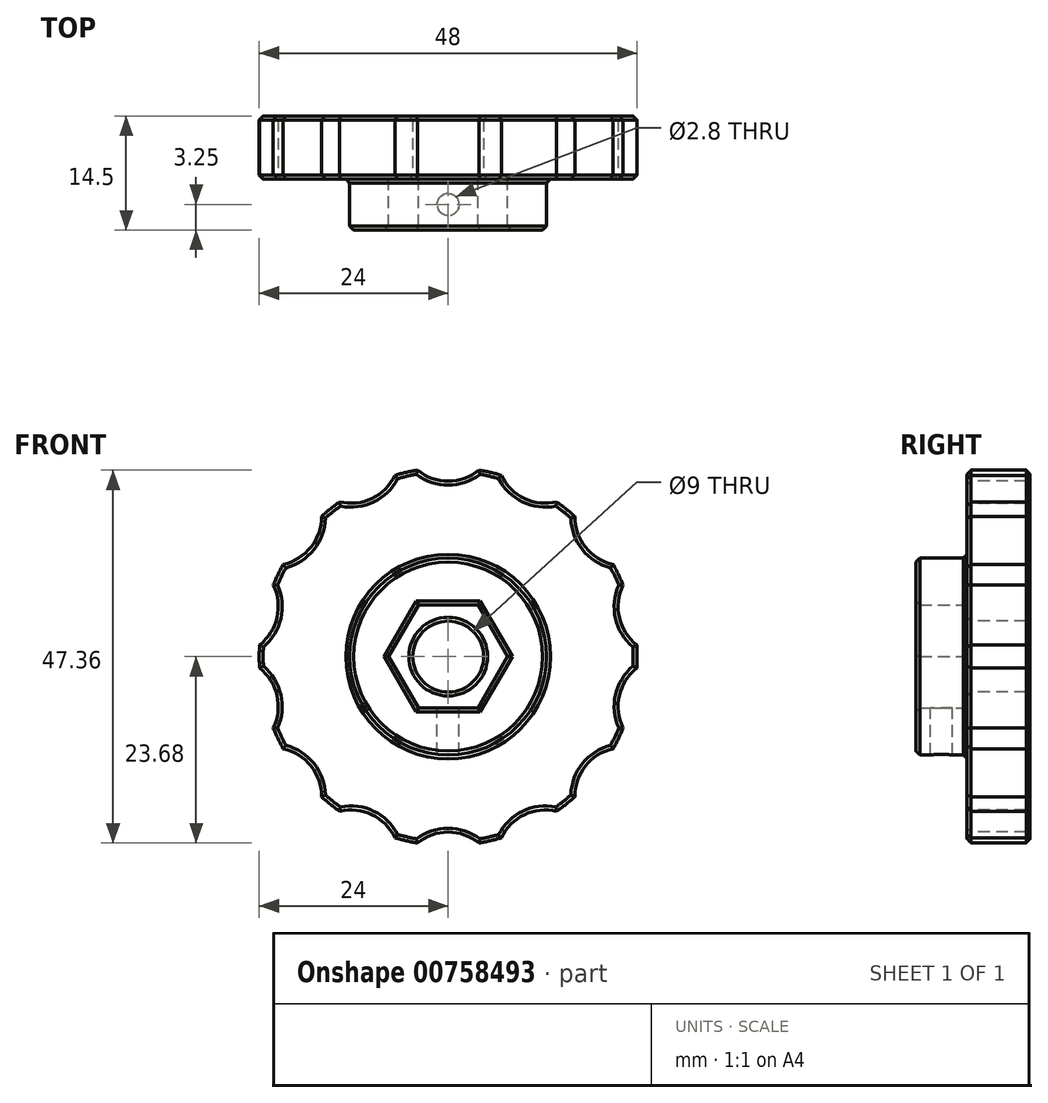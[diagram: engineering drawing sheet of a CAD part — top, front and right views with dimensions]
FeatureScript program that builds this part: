
annotation { "Feature Type Name" : "Feature", "Feature Type Description" : "" }
export const myFeature = defineFeature(function(context is Context, id is Id, definition is map)
    precondition{}
    {
        {
            var Q0;
            Q0=qCreatedBy(makeId("Front.planeOp"),FACE);
            var sketch = newSketch(context, id + "F0", { "sketchPlane" : qUnion([Q0])});
            skCircle(sketch, "E0", {"center": v(0, 0) * mm, "radius": 24 * mm});
            skCircle(sketch, "E1.cCircle", {"center": v(0, 0) * mm, "radius": 6.55 * mm, "construction": true});
            skLineSegment(sketch, "E1.0", {"start": v(-3.78, 6.55) * mm, "end": v(3.78, 6.55) * mm});
            skLineSegment(sketch, "E1.1", {"start": v(3.78, 6.55) * mm, "end": v(7.56, 0) * mm});
            skLineSegment(sketch, "E1.2", {"start": v(7.56, 0) * mm, "end": v(3.78, -6.55) * mm});
            skLineSegment(sketch, "E1.3", {"start": v(3.78, -6.55) * mm, "end": v(-3.78, -6.55) * mm});
            skLineSegment(sketch, "E1.4", {"start": v(-3.78, -6.55) * mm, "end": v(-7.56, 0) * mm});
            skLineSegment(sketch, "E1.5", {"start": v(-7.56, 0) * mm, "end": v(-3.78, 6.55) * mm});
            skPoint(sketch, "E1.0.midPoint", {"position": v(0, 6.55) * mm});
            skCircle(sketch, "E2", {"center": v(0, 0) * mm, "radius": 12.5 * mm});
            skCircle(sketch, "E3", {"center": v(0, 0) * mm, "radius": 4.5 * mm});
            skArc(sketch, "E4", {"start": v(-3.9, 23.68) * mm, "mid": v(0, 22.3) * mm, "end": v(3.9, 23.68) * mm});
            skArc(sketch, "E5.1.0", {"start": v(-13.79, 19.64) * mm, "mid": v(-9.68, 20.1) * mm, "end": v(-6.76, 23.03) * mm});
            skArc(sketch, "E5.2.0", {"start": v(-20.95, 11.72) * mm, "mid": v(-17.44, 13.9) * mm, "end": v(-16.08, 17.81) * mm});
            skArc(sketch, "E5.3.0", {"start": v(-23.96, 1.47) * mm, "mid": v(-21.74, 4.96) * mm, "end": v(-22.22, 9.07) * mm});
            skArc(sketch, "E5.4.0", {"start": v(-22.22, -9.07) * mm, "mid": v(-21.74, -4.96) * mm, "end": v(-23.96, -1.47) * mm});
            skArc(sketch, "E5.5.0", {"start": v(-16.08, -17.81) * mm, "mid": v(-17.44, -13.9) * mm, "end": v(-20.95, -11.72) * mm});
            skArc(sketch, "E5.6.0", {"start": v(-6.76, -23.03) * mm, "mid": v(-9.68, -20.1) * mm, "end": v(-13.79, -19.64) * mm});
            skArc(sketch, "E5.7.0", {"start": v(3.9, -23.68) * mm, "mid": v(0, -22.3) * mm, "end": v(-3.9, -23.68) * mm});
            skArc(sketch, "E5.8.0", {"start": v(13.79, -19.64) * mm, "mid": v(9.68, -20.1) * mm, "end": v(6.76, -23.03) * mm});
            skArc(sketch, "E5.9.0", {"start": v(20.95, -11.72) * mm, "mid": v(17.44, -13.9) * mm, "end": v(16.08, -17.81) * mm});
            skArc(sketch, "E5.10.0", {"start": v(23.96, -1.47) * mm, "mid": v(21.74, -4.96) * mm, "end": v(22.22, -9.07) * mm});
            skArc(sketch, "E5.11.0", {"start": v(22.22, 9.07) * mm, "mid": v(21.74, 4.96) * mm, "end": v(23.96, 1.47) * mm});
            skArc(sketch, "E5.12.0", {"start": v(16.08, 17.81) * mm, "mid": v(17.44, 13.9) * mm, "end": v(20.95, 11.72) * mm});
            skArc(sketch, "E5.13.0", {"start": v(6.76, 23.03) * mm, "mid": v(9.68, 20.1) * mm, "end": v(13.79, 19.64) * mm});
            skSolve(sketch);
        }
        {
            var Q0;
            Q0=makeQuery(id+"F0.imprint","IMPRINT",FACE,{"disambiguationData":[TD([[makeQuery(id+"F0.imprint","IMPRINT",EDGE,{"derivedFrom":sQuery(id+"F0.wireOp",EDGE,"E2")}),-1.0]])]});
            var Q1;
            Q1=makeQuery(id+"F0.imprint","IMPRINT",FACE,{"disambiguationData":[TD([[makeQuery(id+"F0.imprint","IMPRINT",EDGE,{"derivedFrom":sQuery(id+"F0.wireOp",EDGE,"E1.0")}),1.0]])]});
            var Q2;
            Q2=makeQuery(id+"F0.imprint","IMPRINT",FACE,{"disambiguationData":[TD([[makeQuery(id+"F0.imprint","IMPRINT",EDGE,{"derivedFrom":sQuery(id+"F0.wireOp",EDGE,"E1.0")}),-1.0]])]});
            extrude(context, id + "F1", {"entities" : qUnion([Q0, Q1, Q2]), "oppositeDirection" : true, "depth" : (15 - 6.5 - 0.5) * mm, "offsetDistance" : 25 * mm});
        }
        {
            var Q0;
            Q0=makeQuery(id+"F0.imprint","IMPRINT",FACE,{"disambiguationData":[TD([[makeQuery(id+"F0.imprint","IMPRINT",EDGE,{"derivedFrom":sQuery(id+"F0.wireOp",EDGE,"E1.0")}),1.0]])]});
            extrude(context, id + "F2", {"entities" : qUnion([Q0]), "operationType" : NewBodyOperationType.ADD, "depth" : 6.5 * mm, "offsetDistance" : 25 * mm});
        }
        {
            var Q0;
            Q0=makeQuery(id+"F2.opExtrude","SWEPT_FACE",FACE,{"disambiguationData":[OSD([sQuery(id+"F0.wireOp",EDGE,"E1.3")])]});
            var sketch = newSketch(context, id + "F3", { "sketchPlane" : qUnion([Q0])});
            skPoint(sketch, "E6", {"position": v(0, -3.25) * mm});
            skSolve(sketch);
        }
        {
            var Q0;
            Q0=sQuery(id+"F3.wireOp",VERTEX,"E6");
            var Q1;
            Q1=makeQuery(id+"F1.opExtrude","SWEPT_BODY",BODY,{"disambiguationData":[OSD([sQuery(id+"F0.wireOp",EDGE,"E0"),sQuery(id+"F0.wireOp",EDGE,"E3"),sQuery(id+"F0.wireOp",EDGE,"E4"),sQuery(id+"F0.wireOp",EDGE,"E5.1.0"),sQuery(id+"F0.wireOp",EDGE,"E5.2.0"),sQuery(id+"F0.wireOp",EDGE,"E5.3.0"),sQuery(id+"F0.wireOp",EDGE,"E5.4.0"),sQuery(id+"F0.wireOp",EDGE,"E5.5.0"),sQuery(id+"F0.wireOp",EDGE,"E5.6.0"),sQuery(id+"F0.wireOp",EDGE,"E5.7.0"),sQuery(id+"F0.wireOp",EDGE,"E5.8.0"),sQuery(id+"F0.wireOp",EDGE,"E5.9.0"),sQuery(id+"F0.wireOp",EDGE,"E5.10.0"),sQuery(id+"F0.wireOp",EDGE,"E5.11.0"),sQuery(id+"F0.wireOp",EDGE,"E5.12.0"),sQuery(id+"F0.wireOp",EDGE,"E5.13.0")])]});
            hole(context, id + "F4", {"style" : HoleStyle.SIMPLE, "endStyle" : HoleEndStyle.THROUGH, "holeDiameter" : 2.8 * mm, "majorDiameter" : 5 * mm, "isTappedThrough" : true, "tappedDepth" : 12 * mm, "tapClearance" : 3, "locations" : qUnion([Q0]), "scope" : qUnion([Q1])});
        }
        {
            var Q0;
            {var subQ0=sQuery(id+"F0.wireOp",EDGE,"E5.7.0");var subQ1=sQuery(id+"F0.wireOp",EDGE,"E5.5.0");var subQ2=sQuery(id+"F0.wireOp",EDGE,"E5.4.0");var subQ3=sQuery(id+"F0.wireOp",EDGE,"E5.3.0");var subQ4=sQuery(id+"F0.wireOp",EDGE,"E5.2.0");var subQ5=sQuery(id+"F0.wireOp",EDGE,"E5.1.0");var subQ6=sQuery(id+"F0.wireOp",EDGE,"E4");var subQ7=sQuery(id+"F0.wireOp",EDGE,"E5.10.0");var subQ8=sQuery(id+"F0.wireOp",EDGE,"E0");var subQ9=sQuery(id+"F0.wireOp",EDGE,"E5.11.0");var subQ10=sQuery(id+"F0.wireOp",EDGE,"E5.9.0");var subQ11=sQuery(id+"F0.wireOp",EDGE,"E5.8.0");var subQ12=sQuery(id+"F0.wireOp",EDGE,"E5.13.0");var subQ13=sQuery(id+"F0.wireOp",EDGE,"E5.12.0");var subQ14=sQuery(id+"F0.wireOp",EDGE,"E5.6.0");Q0=makeQuery(id+"F2.boolean.opBoolean","SPLIT",FACE,{"disambiguationData":[TD([makeQuery(id+"F1.opExtrude","SWEPT_FACE",FACE,{"disambiguationData":[OSD([subQ6])]})])],"derivedFrom":makeQuery(id+"F1.opExtrude","CAP_FACE",FACE,{"disambiguationData":[OSD([subQ8,sQuery(id+"F0.wireOp",EDGE,"E3"),subQ6,subQ5,subQ4,subQ3,subQ2,subQ1,subQ14,subQ0,subQ11,subQ10,subQ7,subQ9,subQ13,subQ12])],"isStart":true})});}
            var Q1;
            Q1=makeQuery(id+"F1.opExtrude","CAP_FACE",FACE,{"disambiguationData":[OSD([sQuery(id+"F0.wireOp",EDGE,"E0"),sQuery(id+"F0.wireOp",EDGE,"E3"),sQuery(id+"F0.wireOp",EDGE,"E4"),sQuery(id+"F0.wireOp",EDGE,"E5.1.0"),sQuery(id+"F0.wireOp",EDGE,"E5.2.0"),sQuery(id+"F0.wireOp",EDGE,"E5.3.0"),sQuery(id+"F0.wireOp",EDGE,"E5.4.0"),sQuery(id+"F0.wireOp",EDGE,"E5.5.0"),sQuery(id+"F0.wireOp",EDGE,"E5.6.0"),sQuery(id+"F0.wireOp",EDGE,"E5.7.0"),sQuery(id+"F0.wireOp",EDGE,"E5.8.0"),sQuery(id+"F0.wireOp",EDGE,"E5.9.0"),sQuery(id+"F0.wireOp",EDGE,"E5.10.0"),sQuery(id+"F0.wireOp",EDGE,"E5.11.0"),sQuery(id+"F0.wireOp",EDGE,"E5.12.0"),sQuery(id+"F0.wireOp",EDGE,"E5.13.0")])],"isStart":false});
            var Q2;
            Q2=makeQuery(id+"F2.opExtrude","CAP_FACE",FACE,{"disambiguationData":[OSD([sQuery(id+"F0.wireOp",EDGE,"E1.0"),sQuery(id+"F0.wireOp",EDGE,"E1.1"),sQuery(id+"F0.wireOp",EDGE,"E1.2"),sQuery(id+"F0.wireOp",EDGE,"E1.3"),sQuery(id+"F0.wireOp",EDGE,"E1.4"),sQuery(id+"F0.wireOp",EDGE,"E1.5"),sQuery(id+"F0.wireOp",EDGE,"E2")])],"isStart":false});
            var Q3;
            Q3=makeQuery(id+"F1.opExtrude","CAP_EDGE",EDGE,{"disambiguationData":[OSD([sQuery(id+"F0.wireOp",EDGE,"E3")])],"isStart":true});
            chamfer(context, id + "F5", {"entities" : qUnion([Q0, Q1, Q2, Q3]), "width" : 0.5 * mm, "tangentPropagation" : true});
        }
    });
